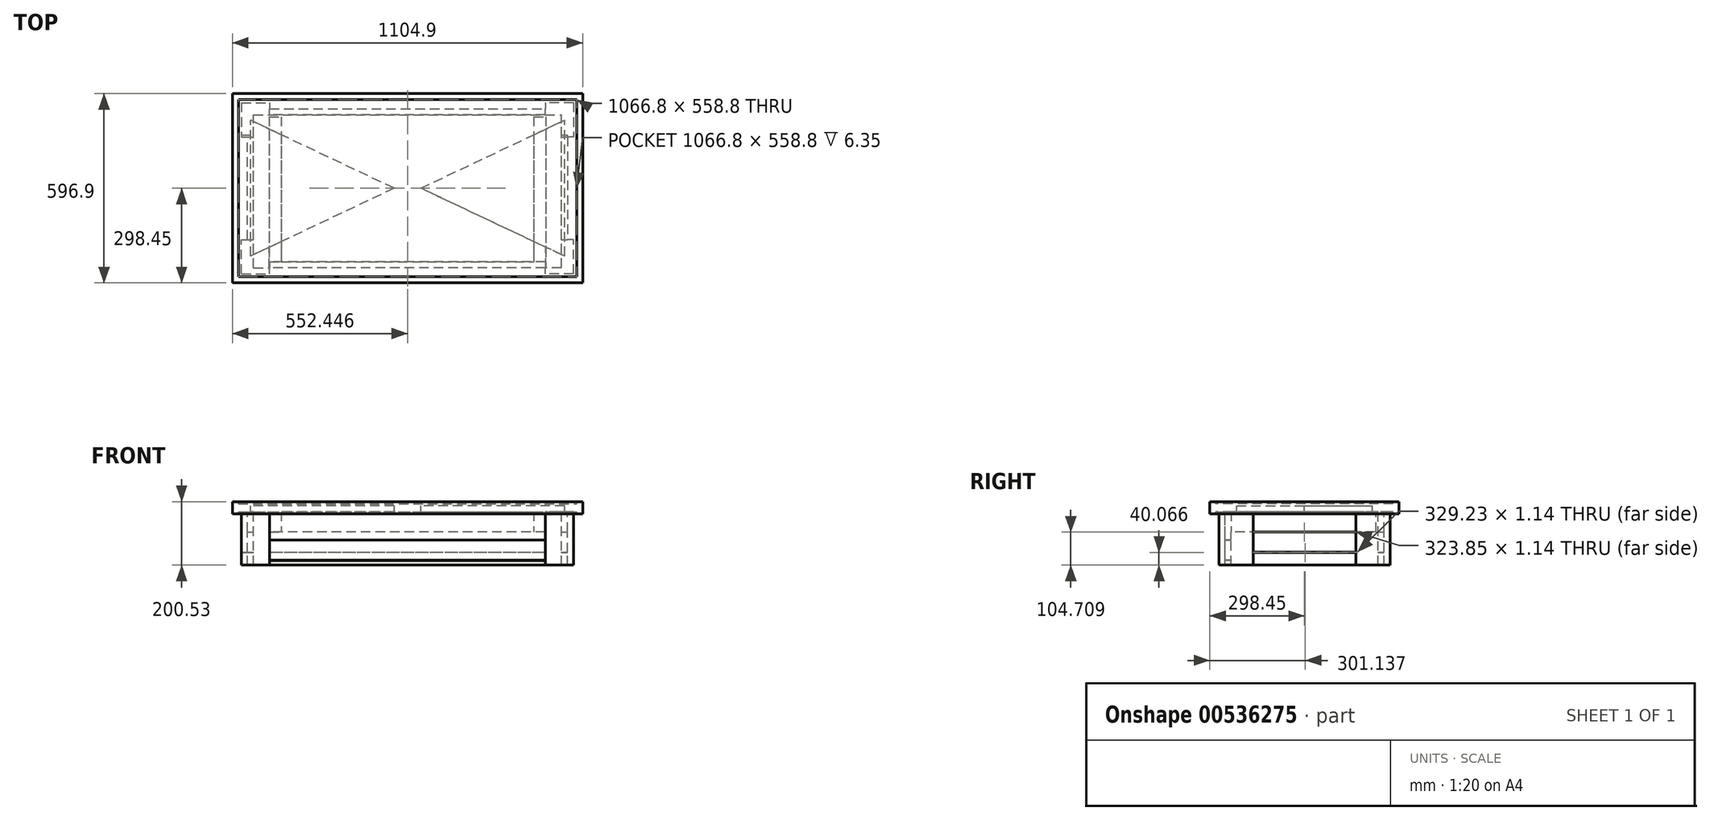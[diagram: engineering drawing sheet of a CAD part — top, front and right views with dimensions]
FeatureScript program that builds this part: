
annotation { "Feature Type Name" : "Feature", "Feature Type Description" : "" }
export const myFeature = defineFeature(function(context is Context, id is Id, definition is map)
    precondition{}
    {
        {
            var Q0;
            Q0=qCreatedBy(makeId("Top.planeOp"),FACE);
            var sketch = newSketch(context, id + "F0", { "sketchPlane" : qUnion([Q0])});
            skLineSegment(sketch, "E0.bottom", {"start": v(-500.95, 298.2) * mm, "end": v(565.85, 298.2) * mm});
            skLineSegment(sketch, "E0.top", {"start": v(-500.95, -260.6) * mm, "end": v(565.85, -260.6) * mm});
            skLineSegment(sketch, "E0.left", {"start": v(-500.95, 298.2) * mm, "end": v(-500.95, -260.6) * mm});
            skLineSegment(sketch, "E0.right", {"start": v(565.85, 298.2) * mm, "end": v(565.85, -260.6) * mm});
            skSolve(sketch);
        }
        {
            var Q0;
            Q0 = qSketchRegion(id + "F0", true);
            extrude(context, id + "F1", {"entities" : qUnion([Q0]), "depth" : 6.35 * mm, "offsetDistance" : 25.4 * mm});
        }
        {
            var Q0;
            Q0=makeQuery(id+"F1.opExtrude","CAP_FACE",FACE,{"disambiguationData":[OSD([sQuery(id+"F0.wireOp",EDGE,"E0.bottom"),sQuery(id+"F0.wireOp",EDGE,"E0.top"),sQuery(id+"F0.wireOp",EDGE,"E0.left"),sQuery(id+"F0.wireOp",EDGE,"E0.right")])],"isStart":false});
            cPlane(context, id + "F2", {"entities" : qUnion([Q0]), "cplaneType" : CPlaneType.OFFSET, "offset" : 6.35 * mm, "width" : 152.4 * mm, "height" : 152.4 * mm});
        }
        {
            var Q0;
            Q0=qCreatedBy(id+"F2.planeOp",FACE);
            var sketch = newSketch(context, id + "F3", { "sketchPlane" : qUnion([Q0])});
            skLineSegment(sketch, "E1.bottom", {"start": v(-520, 317.26) * mm, "end": v(584.9, 317.26) * mm});
            skLineSegment(sketch, "E1.top", {"start": v(-520, -279.64) * mm, "end": v(584.9, -279.64) * mm});
            skLineSegment(sketch, "E1.left", {"start": v(-520, 317.26) * mm, "end": v(-520, -279.64) * mm});
            skLineSegment(sketch, "E1.right", {"start": v(584.9, 317.26) * mm, "end": v(584.9, -279.64) * mm});
            skLineSegment(sketch, "E2.bottom", {"start": v(-500.95, 298.2) * mm, "end": v(565.85, 298.2) * mm});
            skLineSegment(sketch, "E2.top", {"start": v(-500.95, -260.6) * mm, "end": v(565.85, -260.6) * mm});
            skLineSegment(sketch, "E2.left", {"start": v(-500.95, 298.2) * mm, "end": v(-500.95, -260.6) * mm});
            skLineSegment(sketch, "E2.right", {"start": v(565.85, 298.2) * mm, "end": v(565.85, -260.6) * mm});
            skSolve(sketch);
        }
        {
            var Q0;
            Q0 = qSketchRegion(id + "F3", true);
            extrude(context, id + "F4", {"entities" : qUnion([Q0]), "oppositeDirection" : true, "depth" : 38.1 * mm, "offsetDistance" : 25.4 * mm});
        }
        {
            var Q0;
            Q0=makeQuery(id+"F1.opExtrude","CAP_FACE",FACE,{"disambiguationData":[OSD([sQuery(id+"F0.wireOp",EDGE,"E0.bottom"),sQuery(id+"F0.wireOp",EDGE,"E0.top"),sQuery(id+"F0.wireOp",EDGE,"E0.left"),sQuery(id+"F0.wireOp",EDGE,"E0.right")])],"isStart":true});
            var sketch = newSketch(context, id + "F5", { "sketchPlane" : qUnion([Q0])});
            skLineSegment(sketch, "E3.bottom", {"start": v(565.85, 260.6) * mm, "end": v(-500.95, 260.6) * mm});
            skLineSegment(sketch, "E3.top", {"start": v(565.85, -298.2) * mm, "end": v(-500.95, -298.2) * mm});
            skLineSegment(sketch, "E3.left", {"start": v(565.85, 260.6) * mm, "end": v(565.85, -298.2) * mm});
            skLineSegment(sketch, "E3.right", {"start": v(-500.95, 260.6) * mm, "end": v(-500.95, -298.2) * mm});
            skLineSegment(sketch, "E4.bottom", {"start": v(500.82, 222.5) * mm, "end": v(-435.93, 222.5) * mm});
            skLineSegment(sketch, "E4.top", {"start": v(500.82, -260.1) * mm, "end": v(-435.93, -260.1) * mm});
            skLineSegment(sketch, "E4.left", {"start": v(527.75, 195.57) * mm, "end": v(527.75, -233.19) * mm});
            skLineSegment(sketch, "E4.right", {"start": v(-462.85, 195.57) * mm, "end": v(-462.85, -233.19) * mm});
            skLineSegment(sketch, "E5", {"start": v(527.75, 195.57) * mm, "end": v(74.38, -18.8) * mm});
            skLineSegment(sketch, "E6", {"start": v(500.82, 222.5) * mm, "end": v(32.45, 1.02) * mm});
            skLineSegment(sketch, "E7", {"start": v(-435.93, 222.5) * mm, "end": v(32.45, 1.02) * mm});
            skLineSegment(sketch, "E8", {"start": v(500.82, -260.1) * mm, "end": v(32.45, -38.64) * mm});
            skLineSegment(sketch, "E9.trimOffspring", {"start": v(-9.49, -18.8) * mm, "end": v(-462.85, 195.57) * mm});
            skLineSegment(sketch, "E10.trimOffspring", {"start": v(74.38, -18.8) * mm, "end": v(527.75, -233.19) * mm});
            skLineSegment(sketch, "E11.trimOffspring", {"start": v(32.45, -38.64) * mm, "end": v(-435.93, -260.1) * mm});
            skLineSegment(sketch, "E12.trimOffspring", {"start": v(-9.49, -18.8) * mm, "end": v(-462.85, -233.19) * mm});
            skPoint(sketch, "E13.orphan", {"position": v(-462.85, -260.1) * mm});
            skPoint(sketch, "E14.orphan", {"position": v(527.75, 222.5) * mm});
            skPoint(sketch, "E15.orphan", {"position": v(527.75, -260.1) * mm});
            skPoint(sketch, "E16.orphan", {"position": v(-462.85, 222.5) * mm});
            skSolve(sketch);
        }
        {
            var Q0;
            Q0=makeQuery(id+"F5.imprint","IMPRINT",FACE,{"disambiguationData":[TD([[makeQuery(id+"F5.imprint","IMPRINT",EDGE,{"derivedFrom":sQuery(id+"F5.wireOp",EDGE,"E3.bottom")}),-1.0]])]});
            extrude(context, id + "F6", {"entities" : qUnion([Q0]), "depth" : 19.05 * mm, "offsetDistance" : 25.4 * mm});
        }
        {
            var Q0;
            Q0=makeQuery(id+"F6.opExtrude","CAP_FACE",FACE,{"disambiguationData":[OSD([sQuery(id+"F5.wireOp",EDGE,"E3.bottom"),sQuery(id+"F5.wireOp",EDGE,"E3.top"),sQuery(id+"F5.wireOp",EDGE,"E3.left"),sQuery(id+"F5.wireOp",EDGE,"E3.right"),sQuery(id+"F5.wireOp",EDGE,"E4.bottom"),sQuery(id+"F5.wireOp",EDGE,"E4.top"),sQuery(id+"F5.wireOp",EDGE,"E4.left"),sQuery(id+"F5.wireOp",EDGE,"E4.right"),sQuery(id+"F5.wireOp",EDGE,"E5"),sQuery(id+"F5.wireOp",EDGE,"E6"),sQuery(id+"F5.wireOp",EDGE,"E7"),sQuery(id+"F5.wireOp",EDGE,"E8"),sQuery(id+"F5.wireOp",EDGE,"E9.trimOffspring"),sQuery(id+"F5.wireOp",EDGE,"E10.trimOffspring"),sQuery(id+"F5.wireOp",EDGE,"E11.trimOffspring"),sQuery(id+"F5.wireOp",EDGE,"E12.trimOffspring")])],"isStart":false});
            var sketch = newSketch(context, id + "F7", { "sketchPlane" : qUnion([Q0])});
            skLineSegment(sketch, "E17.bottom", {"start": v(-403.8, 232.02) * mm, "end": v(468.7, 232.02) * mm});
            skLineSegment(sketch, "E17.top", {"start": v(-403.8, 212.97) * mm, "end": v(468.7, 212.97) * mm});
            skLineSegment(sketch, "E17.left", {"start": v(-403.8, 232.02) * mm, "end": v(-403.8, 212.97) * mm});
            skLineSegment(sketch, "E17.right", {"start": v(468.7, 232.02) * mm, "end": v(468.7, 212.97) * mm});
            skSolve(sketch);
        }
        {
            var Q0;
            Q0 = qSketchRegion(id + "F7", true);
            extrude(context, id + "F8", {"entities" : qUnion([Q0]), "operationType" : NewBodyOperationType.ADD, "depth" : 88.9 * mm, "offsetDistance" : 25.4 * mm});
        }
        {
            var Q0;
            Q0=makeQuery(id+"F8.opExtrude","SWEPT_FACE",FACE,{"disambiguationData":[OSD([sQuery(id+"F7.wireOp",EDGE,"E17.top")])]});
            var sketch = newSketch(context, id + "F9", { "sketchPlane" : qUnion([Q0])});
            skLineSegment(sketch, "E18.bottom", {"start": v(403.8, -19.05) * mm, "end": v(365.7, -19.05) * mm});
            skLineSegment(sketch, "E18.top", {"start": v(403.8, -82.55) * mm, "end": v(365.7, -82.55) * mm});
            skLineSegment(sketch, "E18.left", {"start": v(403.8, -19.05) * mm, "end": v(403.8, -82.55) * mm});
            skLineSegment(sketch, "E18.right", {"start": v(365.7, -19.05) * mm, "end": v(365.7, -82.55) * mm});
            skLineSegment(sketch, "E19.bottom", {"start": v(-468.7, -19.05) * mm, "end": v(-430.6, -19.05) * mm});
            skLineSegment(sketch, "E19.top", {"start": v(-468.7, -82.55) * mm, "end": v(-430.6, -82.55) * mm});
            skLineSegment(sketch, "E19.left", {"start": v(-468.7, -19.05) * mm, "end": v(-468.7, -82.55) * mm});
            skLineSegment(sketch, "E19.right", {"start": v(-430.6, -19.05) * mm, "end": v(-430.6, -82.55) * mm});
            skSolve(sketch);
        }
        {
            var Q0;
            Q0 = qSketchRegion(id + "F9", true);
            extrude(context, id + "F10", {"entities" : qUnion([Q0]), "operationType" : NewBodyOperationType.ADD, "depth" : 457.2 * mm, "offsetDistance" : 25.4 * mm});
        }
        {
            var Q0;
            {var subQ2=sQuery(id+"F5.wireOp",EDGE,"E12.trimOffspring");var subQ3=sQuery(id+"F5.wireOp",EDGE,"E11.trimOffspring");var subQ4=sQuery(id+"F5.wireOp",EDGE,"E10.trimOffspring");var subQ5=sQuery(id+"F5.wireOp",EDGE,"E9.trimOffspring");var subQ6=sQuery(id+"F5.wireOp",EDGE,"E8");var subQ7=sQuery(id+"F5.wireOp",EDGE,"E7");var subQ9=sQuery(id+"F5.wireOp",EDGE,"E3.left");var subQ10=sQuery(id+"F5.wireOp",EDGE,"E3.top");var subQ13=sQuery(id+"F5.wireOp",EDGE,"E3.right");var subQ14=sQuery(id+"F5.wireOp",EDGE,"E3.bottom");var subQ15=sQuery(id+"F5.wireOp",EDGE,"E6");var subQ16=sQuery(id+"F5.wireOp",EDGE,"E4.bottom");var subQ17=sQuery(id+"F5.wireOp",EDGE,"E4.top");var subQ18=sQuery(id+"F5.wireOp",EDGE,"E4.left");var subQ19=sQuery(id+"F5.wireOp",EDGE,"E4.right");var subQ20=sQuery(id+"F5.wireOp",EDGE,"E5");Q0=makeQuery(id+"F10.boolean.opBoolean","SPLIT",FACE,{"disambiguationData":[TD([makeQuery(id+"F6.opExtrude","SWEPT_FACE",FACE,{"disambiguationData":[OSD([subQ14])]})])],"derivedFrom":makeQuery(id+"F6.opExtrude","CAP_FACE",FACE,{"disambiguationData":[OSD([subQ14,subQ10,subQ9,subQ13,subQ16,subQ17,subQ18,subQ19,subQ20,subQ15,subQ7,subQ6,subQ5,subQ4,subQ3,subQ2])],"isStart":false})});}
            var sketch = newSketch(context, id + "F11", { "sketchPlane" : qUnion([Q0])});
            skLineSegment(sketch, "E20.bottom", {"start": v(-491.43, 251.07) * mm, "end": v(-402.53, 251.07) * mm});
            skLineSegment(sketch, "E20.top", {"start": v(-491.43, 232.02) * mm, "end": v(-402.53, 232.02) * mm});
            skLineSegment(sketch, "E20.left", {"start": v(-491.43, 251.07) * mm, "end": v(-491.43, 232.02) * mm});
            skLineSegment(sketch, "E20.right", {"start": v(-402.53, 251.07) * mm, "end": v(-402.53, 232.02) * mm});
            skLineSegment(sketch, "E21.bottom", {"start": v(-491.43, 232.02) * mm, "end": v(-472.38, 232.02) * mm});
            skLineSegment(sketch, "E21.top", {"start": v(-491.43, 143.12) * mm, "end": v(-472.38, 143.12) * mm});
            skLineSegment(sketch, "E21.left", {"start": v(-491.43, 232.02) * mm, "end": v(-491.43, 143.12) * mm});
            skLineSegment(sketch, "E21.right", {"start": v(-472.38, 232.02) * mm, "end": v(-472.38, 143.12) * mm});
            skLineSegment(sketch, "E22", {"start": v(-9.49, -18.8) * mm, "end": v(32.45, -18.8) * mm});
            skLineSegment(sketch, "E23", {"start": v(32.45, -18.8) * mm, "end": v(32.45, 108.2) * mm});
            skLineSegment(sketch, "E24.MirrorCS", {"start": v(-491.43, -288.68) * mm, "end": v(-491.43, -269.63) * mm});
            skLineSegment(sketch, "E25.MirrorCS", {"start": v(-491.43, -269.63) * mm, "end": v(-472.38, -269.63) * mm});
            skLineSegment(sketch, "E26.MirrorCS", {"start": v(-472.38, -269.63) * mm, "end": v(-472.38, -180.73) * mm});
            skLineSegment(sketch, "E27.MirrorCS", {"start": v(-491.43, -180.73) * mm, "end": v(-472.38, -180.73) * mm});
            skLineSegment(sketch, "E28.MirrorCS", {"start": v(-491.43, -269.63) * mm, "end": v(-491.43, -180.73) * mm});
            skLineSegment(sketch, "E29.MirrorCS", {"start": v(-491.43, -269.63) * mm, "end": v(-402.53, -269.63) * mm});
            skLineSegment(sketch, "E30.MirrorCS", {"start": v(-402.53, -288.68) * mm, "end": v(-402.53, -269.63) * mm});
            skLineSegment(sketch, "E31.MirrorCS", {"start": v(-491.43, -288.68) * mm, "end": v(-402.53, -288.68) * mm});
            skLineSegment(sketch, "E32.MirrorCS", {"start": v(556.32, -288.68) * mm, "end": v(467.42, -288.68) * mm});
            skLineSegment(sketch, "E33.MirrorCS", {"start": v(556.32, -288.68) * mm, "end": v(556.32, -269.63) * mm});
            skLineSegment(sketch, "E34.MirrorCS", {"start": v(556.32, -269.63) * mm, "end": v(467.42, -269.63) * mm});
            skLineSegment(sketch, "E35.MirrorCS", {"start": v(467.42, -288.68) * mm, "end": v(467.42, -269.63) * mm});
            skLineSegment(sketch, "E36.MirrorCS", {"start": v(537.27, -269.63) * mm, "end": v(537.27, -180.73) * mm});
            skLineSegment(sketch, "E37.MirrorCS", {"start": v(556.32, -269.63) * mm, "end": v(556.32, -180.73) * mm});
            skLineSegment(sketch, "E38.MirrorCS", {"start": v(556.32, -180.73) * mm, "end": v(537.27, -180.73) * mm});
            skLineSegment(sketch, "E39.MirrorCS", {"start": v(556.32, 143.12) * mm, "end": v(537.27, 143.12) * mm});
            skLineSegment(sketch, "E40.MirrorCS", {"start": v(556.32, 232.02) * mm, "end": v(556.32, 143.12) * mm});
            skLineSegment(sketch, "E41.MirrorCS", {"start": v(537.27, 232.02) * mm, "end": v(537.27, 143.12) * mm});
            skLineSegment(sketch, "E42.MirrorCS", {"start": v(556.32, 232.02) * mm, "end": v(467.42, 232.02) * mm});
            skLineSegment(sketch, "E43.MirrorCS", {"start": v(556.32, 251.07) * mm, "end": v(467.42, 251.07) * mm});
            skLineSegment(sketch, "E44.MirrorCS", {"start": v(556.32, 251.07) * mm, "end": v(556.32, 232.02) * mm});
            skLineSegment(sketch, "E45.MirrorCS", {"start": v(467.42, 251.07) * mm, "end": v(467.42, 232.02) * mm});
            skSolve(sketch);
        }
        {
            var Q0;
            Q0 = qSketchRegion(id + "F11", true);
            extrude(context, id + "F12", {"entities" : qUnion([Q0]), "operationType" : NewBodyOperationType.ADD, "depth" : 419.1 * mm, "offsetDistance" : 25.4 * mm});
        }
        {
            var Q0;
            {var subQ2=sQuery(id+"F5.wireOp",EDGE,"E12.trimOffspring");var subQ3=sQuery(id+"F5.wireOp",EDGE,"E11.trimOffspring");var subQ4=sQuery(id+"F5.wireOp",EDGE,"E10.trimOffspring");var subQ5=sQuery(id+"F5.wireOp",EDGE,"E9.trimOffspring");var subQ6=sQuery(id+"F5.wireOp",EDGE,"E8");var subQ7=sQuery(id+"F5.wireOp",EDGE,"E7");var subQ9=sQuery(id+"F5.wireOp",EDGE,"E3.left");var subQ10=sQuery(id+"F5.wireOp",EDGE,"E3.top");var subQ13=sQuery(id+"F5.wireOp",EDGE,"E3.right");var subQ14=sQuery(id+"F5.wireOp",EDGE,"E3.bottom");var subQ15=sQuery(id+"F5.wireOp",EDGE,"E6");var subQ16=sQuery(id+"F5.wireOp",EDGE,"E4.bottom");var subQ17=sQuery(id+"F5.wireOp",EDGE,"E4.top");var subQ18=sQuery(id+"F5.wireOp",EDGE,"E4.left");var subQ19=sQuery(id+"F5.wireOp",EDGE,"E4.right");var subQ20=sQuery(id+"F5.wireOp",EDGE,"E5");Q0=makeQuery(id+"F10.boolean.opBoolean","SPLIT",FACE,{"disambiguationData":[TD([makeQuery(id+"F6.opExtrude","SWEPT_FACE",FACE,{"disambiguationData":[OSD([subQ14])]})])],"derivedFrom":makeQuery(id+"F6.opExtrude","CAP_FACE",FACE,{"disambiguationData":[OSD([subQ14,subQ10,subQ9,subQ13,subQ16,subQ17,subQ18,subQ19,subQ20,subQ15,subQ7,subQ6,subQ5,subQ4,subQ3,subQ2])],"isStart":false})});}
            var sketch = newSketch(context, id + "F13", { "sketchPlane" : qUnion([Q0])});
            skLineSegment(sketch, "E46.bottom", {"start": v(-472.38, 232.02) * mm, "end": v(-453.33, 232.02) * mm});
            skLineSegment(sketch, "E46.top", {"start": v(-472.38, -269.63) * mm, "end": v(537.27, -269.63) * mm});
            skLineSegment(sketch, "E46.left", {"start": v(-472.38, 232.02) * mm, "end": v(-472.38, -269.63) * mm});
            skLineSegment(sketch, "E46.right", {"start": v(537.27, 232.02) * mm, "end": v(537.27, -269.63) * mm});
            skLineSegment(sketch, "E47.top", {"start": v(-453.33, -250.58) * mm, "end": v(518.22, -250.58) * mm});
            skLineSegment(sketch, "E47.left", {"start": v(-453.33, 212.97) * mm, "end": v(-453.33, -250.58) * mm});
            skLineSegment(sketch, "E47.right", {"start": v(518.22, 212.97) * mm, "end": v(518.22, -250.58) * mm});
            skLineSegment(sketch, "E48", {"start": v(518.22, 212.97) * mm, "end": v(518.22, 232.02) * mm});
            skLineSegment(sketch, "E49", {"start": v(-453.33, 212.97) * mm, "end": v(-453.33, 232.02) * mm});
            skLineSegment(sketch, "E50.trimOffspring", {"start": v(518.22, 232.02) * mm, "end": v(537.27, 232.02) * mm});
            skSolve(sketch);
        }
        {
            var Q0;
            Q0 = qSketchRegion(id + "F13", true);
            extrude(context, id + "F14", {"entities" : qUnion([Q0]), "operationType" : NewBodyOperationType.ADD, "depth" : 192.79 * mm, "offsetDistance" : 25.4 * mm});
        }
        {
            var Q0;
            Q0=makeQuery(id+"F14.opExtrude","SWEPT_FACE",FACE,{"disambiguationData":[OSD([sQuery(id+"F13.wireOp",EDGE,"E46.right")])]});
            var sketch = newSketch(context, id + "F15", { "sketchPlane" : qUnion([Q0])});
            skLineSegment(sketch, "E51.bottom", {"start": v(-143.12, -82.55) * mm, "end": v(180.73, -82.55) * mm});
            skLineSegment(sketch, "E51.top", {"start": v(-143.12, -83.7) * mm, "end": v(180.73, -83.7) * mm});
            skLineSegment(sketch, "E51.left", {"start": v(-143.12, -82.55) * mm, "end": v(-143.12, -83.7) * mm});
            skLineSegment(sketch, "E51.right", {"start": v(180.73, -82.55) * mm, "end": v(180.73, -83.7) * mm});
            skLineSegment(sketch, "E52.bottom", {"start": v(-143.12, -147.2) * mm, "end": v(186.1, -147.2) * mm});
            skLineSegment(sketch, "E52.top", {"start": v(-143.12, -148.34) * mm, "end": v(186.1, -148.34) * mm});
            skLineSegment(sketch, "E52.left", {"start": v(-143.12, -147.2) * mm, "end": v(-143.12, -148.34) * mm});
            skLineSegment(sketch, "E52.right", {"start": v(186.1, -147.2) * mm, "end": v(186.1, -148.34) * mm});
            skSolve(sketch);
        }
        {
            var Q0;
            Q0 = qSketchRegion(id + "F15", true);
            extrude(context, id + "F16", {"entities" : qUnion([Q0]), "operationType" : NewBodyOperationType.REMOVE, "oppositeDirection" : true, "depth" : 1219.2 * mm, "offsetDistance" : 25.4 * mm});
        }
        {
            var Q0;
            Q0=makeQuery(id+"F14.opExtrude","SWEPT_FACE",FACE,{"disambiguationData":[OSD([sQuery(id+"F13.wireOp",EDGE,"E46.top")])]});
            var sketch = newSketch(context, id + "F17", { "sketchPlane" : qUnion([Q0])});
            skLineSegment(sketch, "E53.bottom", {"start": v(-467.42, -147.2) * mm, "end": v(402.53, -147.2) * mm});
            skLineSegment(sketch, "E53.top", {"start": v(-467.42, -148.34) * mm, "end": v(402.53, -148.34) * mm});
            skLineSegment(sketch, "E53.left", {"start": v(-467.42, -148.34) * mm, "end": v(-467.42, -147.2) * mm});
            skLineSegment(sketch, "E53.right", {"start": v(402.53, -148.34) * mm, "end": v(402.53, -147.2) * mm});
            skLineSegment(sketch, "E54.right", {"start": v(402.53, -84.96) * mm, "end": v(402.53, -115.44) * mm});
            skLineSegment(sketch, "E55.bottom", {"start": v(402.53, -82.55) * mm, "end": v(-467.42, -82.55) * mm});
            skLineSegment(sketch, "E55.top", {"start": v(402.53, -83.7) * mm, "end": v(-467.42, -83.7) * mm});
            skLineSegment(sketch, "E55.left", {"start": v(402.53, -82.55) * mm, "end": v(402.53, -83.7) * mm});
            skLineSegment(sketch, "E55.right", {"start": v(-467.42, -82.55) * mm, "end": v(-467.42, -83.7) * mm});
            skSolve(sketch);
        }
        {
            var Q0;
            Q0 = qSketchRegion(id + "F17", true);
            extrude(context, id + "F18", {"entities" : qUnion([Q0]), "operationType" : NewBodyOperationType.REMOVE, "oppositeDirection" : true, "depth" : 25.4 * mm, "offsetDistance" : 25.4 * mm});
        }
        {
            var Q0;
            Q0=makeQuery(id+"F8.opExtrude","CAP_FACE",FACE,{"disambiguationData":[OSD([sQuery(id+"F7.wireOp",EDGE,"E17.bottom"),sQuery(id+"F7.wireOp",EDGE,"E17.top"),sQuery(id+"F7.wireOp",EDGE,"E17.left"),sQuery(id+"F7.wireOp",EDGE,"E17.right")])],"isStart":false});
            cPlane(context, id + "F19", {"entities" : qUnion([Q0]), "cplaneType" : CPlaneType.OFFSET, "offset" : 1.14 * mm, "width" : 152.4 * mm, "height" : 152.4 * mm});
        }
        {
            var Q0;
            Q0=qCreatedBy(id+"F19.planeOp",FACE);
            var sketch = newSketch(context, id + "F20", { "sketchPlane" : qUnion([Q0])});
            skLineSegment(sketch, "E56.bottom", {"start": v(468.7, 212.97) * mm, "end": v(-403.8, 212.97) * mm});
            skLineSegment(sketch, "E56.top", {"start": v(468.7, 232.02) * mm, "end": v(-403.8, 232.02) * mm});
            skLineSegment(sketch, "E56.left", {"start": v(468.7, 212.97) * mm, "end": v(468.7, 232.02) * mm});
            skLineSegment(sketch, "E56.right", {"start": v(-403.8, 212.97) * mm, "end": v(-403.8, 232.02) * mm});
            skSolve(sketch);
        }
        {
            var Q0;
            Q0 = qSketchRegion(id + "F20", true);
            extrude(context, id + "F21", {"entities" : qUnion([Q0]), "operationType" : NewBodyOperationType.ADD, "depth" : 128.14 * mm, "offsetDistance" : 25.4 * mm});
        }
        {
            var Q0;
            Q0=makeQuery(id+"F21.opExtrude","SWEPT_FACE",FACE,{"disambiguationData":[OSD([sQuery(id+"F20.wireOp",EDGE,"E56.top")])]});
            var sketch = newSketch(context, id + "F22", { "sketchPlane" : qUnion([Q0])});
            skLineSegment(sketch, "E57.bottom", {"start": v(-402.53, -172.6) * mm, "end": v(467.42, -172.6) * mm});
            skLineSegment(sketch, "E57.top", {"start": v(-402.53, -173.74) * mm, "end": v(467.42, -173.74) * mm});
            skLineSegment(sketch, "E57.left", {"start": v(-402.53, -172.6) * mm, "end": v(-402.53, -173.74) * mm});
            skLineSegment(sketch, "E57.right", {"start": v(467.42, -172.6) * mm, "end": v(467.42, -173.74) * mm});
            skSolve(sketch);
        }
        {
            var Q0;
            Q0 = qSketchRegion(id + "F22", true);
            extrude(context, id + "F23", {"entities" : qUnion([Q0]), "operationType" : NewBodyOperationType.REMOVE, "oppositeDirection" : true, "depth" : 25.4 * mm, "offsetDistance" : 25.4 * mm});
        }
        {
            var Q0;
            Q0=makeQuery(id+"F14.opExtrude","CAP_FACE",FACE,{"disambiguationData":[OSD([sQuery(id+"F13.wireOp",EDGE,"E46.bottom"),sQuery(id+"F13.wireOp",EDGE,"E46.top"),sQuery(id+"F13.wireOp",EDGE,"E46.left"),sQuery(id+"F13.wireOp",EDGE,"E46.right"),sQuery(id+"F13.wireOp",EDGE,"E47.top"),sQuery(id+"F13.wireOp",EDGE,"E47.left"),sQuery(id+"F13.wireOp",EDGE,"E47.right"),sQuery(id+"F13.wireOp",EDGE,"E48"),sQuery(id+"F13.wireOp",EDGE,"E49"),sQuery(id+"F13.wireOp",EDGE,"E50.trimOffspring")])],"isStart":false});
            var sketch = newSketch(context, id + "F24", { "sketchPlane" : qUnion([Q0])});
            skLineSegment(sketch, "E58.bottom", {"start": v(-472.38, -269.63) * mm, "end": v(-434.28, -269.63) * mm});
            skLineSegment(sketch, "E58.top", {"start": v(-472.38, -180.73) * mm, "end": v(-434.28, -180.73) * mm});
            skLineSegment(sketch, "E58.left", {"start": v(-472.38, -269.63) * mm, "end": v(-472.38, -180.73) * mm});
            skLineSegment(sketch, "E58.right", {"start": v(-434.28, -269.63) * mm, "end": v(-434.28, -180.73) * mm});
            skLineSegment(sketch, "E59.bottom", {"start": v(-472.38, 232.02) * mm, "end": v(-434.28, 232.02) * mm});
            skLineSegment(sketch, "E59.top", {"start": v(-472.38, 143.12) * mm, "end": v(-434.28, 143.12) * mm});
            skLineSegment(sketch, "E59.left", {"start": v(-472.38, 232.02) * mm, "end": v(-472.38, 143.12) * mm});
            skLineSegment(sketch, "E59.right", {"start": v(-434.28, 232.02) * mm, "end": v(-434.28, 143.12) * mm});
            skLineSegment(sketch, "E60.bottom", {"start": v(537.27, -269.63) * mm, "end": v(499.17, -269.63) * mm});
            skLineSegment(sketch, "E60.top", {"start": v(537.27, -180.73) * mm, "end": v(499.17, -180.73) * mm});
            skLineSegment(sketch, "E60.left", {"start": v(537.27, -269.63) * mm, "end": v(537.27, -180.73) * mm});
            skLineSegment(sketch, "E60.right", {"start": v(499.17, -269.63) * mm, "end": v(499.17, -180.73) * mm});
            skLineSegment(sketch, "E61.bottom", {"start": v(537.27, 232.02) * mm, "end": v(499.17, 232.02) * mm});
            skLineSegment(sketch, "E61.top", {"start": v(537.27, 143.12) * mm, "end": v(499.17, 143.12) * mm});
            skLineSegment(sketch, "E61.left", {"start": v(537.27, 232.02) * mm, "end": v(537.27, 143.12) * mm});
            skLineSegment(sketch, "E61.right", {"start": v(499.17, 232.02) * mm, "end": v(499.17, 143.12) * mm});
            skSolve(sketch);
        }
        {
            var Q0;
            Q0 = qSketchRegion(id + "F24", true);
            var Q1;
            Q1=makeQuery(id+"F12.opExtrude","CAP_FACE",FACE,{"disambiguationData":[OSD([sQuery(id+"F11.wireOp",EDGE,"E39.MirrorCS"),sQuery(id+"F11.wireOp",EDGE,"E40.MirrorCS"),sQuery(id+"F11.wireOp",EDGE,"E41.MirrorCS"),sQuery(id+"F11.wireOp",EDGE,"E42.MirrorCS"),sQuery(id+"F11.wireOp",EDGE,"E43.MirrorCS"),sQuery(id+"F11.wireOp",EDGE,"E44.MirrorCS"),sQuery(id+"F11.wireOp",EDGE,"E45.MirrorCS")])],"isStart":false});
            extrude(context, id + "F25", {"entities" : qUnion([Q0]), "operationType" : NewBodyOperationType.ADD, "endBound" : BoundingType.UP_TO_SURFACE, "depth" : 25.4 * mm, "endBoundEntityFace" : qUnion([Q1]), "offsetDistance" : 25.4 * mm});
        }
        {
            var Q0;
            Q0=makeQuery(id+"F12.opExtrude","SWEPT_FACE",FACE,{"disambiguationData":[OSD([sQuery(id+"F11.wireOp",EDGE,"E24.MirrorCS"),sQuery(id+"F11.wireOp",EDGE,"E28.MirrorCS")])]});
            var sketch = newSketch(context, id + "F26", { "sketchPlane" : qUnion([Q0])});
            skLineSegment(sketch, "E62.bottom", {"start": v(-295.03, -187.83) * mm, "end": v(263.77, -187.83) * mm});
            skLineSegment(sketch, "E62.top", {"start": v(-295.03, -568.83) * mm, "end": v(263.77, -568.83) * mm});
            skLineSegment(sketch, "E62.left", {"start": v(-295.03, -187.83) * mm, "end": v(-295.03, -568.83) * mm});
            skLineSegment(sketch, "E62.right", {"start": v(263.77, -187.83) * mm, "end": v(263.77, -568.83) * mm});
            skSolve(sketch);
        }
        {
            var Q0;
            Q0 = qSketchRegion(id + "F26", true);
            extrude(context, id + "F27", {"entities" : qUnion([Q0]), "operationType" : NewBodyOperationType.REMOVE, "oppositeDirection" : true, "depth" : 1397 * mm, "offsetDistance" : 25.4 * mm});
        }
        {
            var Q0;
            {var subQ1=sQuery(id+"F5.wireOp",EDGE,"E4.left");var subQ5=sQuery(id+"F5.wireOp",EDGE,"E4.bottom");var subQ6=makeQuery(id+"F5.imprint","INTERSECT",VERTEX,{"derivedFrom":[subQ5,subQ1]});Q0=makeQuery(id+"F5.imprint","IMPRINT",FACE,{"disambiguationData":[TD([[makeQuery(id+"F5.imprint","IMPRINT",EDGE,{"disambiguationData":[TD([[subQ6,-1.0]])],"derivedFrom":subQ5}),1.0]])]});}
            var Q1;
            {var subQ1=sQuery(id+"F5.wireOp",EDGE,"E4.left");var subQ7=sQuery(id+"F5.wireOp",EDGE,"E4.top");var subQ8=makeQuery(id+"F5.imprint","INTERSECT",VERTEX,{"derivedFrom":[subQ7,subQ1]});Q1=makeQuery(id+"F5.imprint","IMPRINT",FACE,{"disambiguationData":[TD([[makeQuery(id+"F5.imprint","IMPRINT",EDGE,{"disambiguationData":[TD([[subQ8,-1.0]])],"derivedFrom":subQ7}),-1.0]])]});}
            var Q2;
            {var subQ1=sQuery(id+"F5.wireOp",EDGE,"E4.right");var subQ6=sQuery(id+"F5.wireOp",EDGE,"E4.top");var subQ9=makeQuery(id+"F5.imprint","INTERSECT",VERTEX,{"derivedFrom":[subQ6,subQ1]});Q2=makeQuery(id+"F5.imprint","IMPRINT",FACE,{"disambiguationData":[TD([[makeQuery(id+"F5.imprint","IMPRINT",EDGE,{"disambiguationData":[TD([[subQ9,1.0]])],"derivedFrom":subQ6}),-1.0]])]});}
            var Q3;
            {var subQ1=sQuery(id+"F5.wireOp",EDGE,"E4.bottom");var subQ7=sQuery(id+"F5.wireOp",EDGE,"E4.right");var subQ8=makeQuery(id+"F5.imprint","INTERSECT",VERTEX,{"derivedFrom":[subQ1,subQ7]});Q3=makeQuery(id+"F5.imprint","IMPRINT",FACE,{"disambiguationData":[TD([[makeQuery(id+"F5.imprint","IMPRINT",EDGE,{"disambiguationData":[TD([[subQ8,1.0]])],"derivedFrom":subQ1}),1.0]])]});}
            var Q4;
            {var subQ0=sQuery(id+"F5.wireOp",EDGE,"E7");var subQ1=sQuery(id+"F5.wireOp",EDGE,"E5");var subQ2=makeQuery(id+"F5.imprint","INTERSECT",VERTEX,{"derivedFrom":[subQ1,subQ0]});Q4=makeQuery(id+"F5.imprint","IMPRINT",FACE,{"disambiguationData":[TD([[makeQuery(id+"F5.imprint","IMPRINT",EDGE,{"disambiguationData":[TD([[subQ2,-1.0]])],"derivedFrom":subQ1}),-1.0]])]});}
            extrude(context, id + "F28", {"entities" : qUnion([Q0, Q1, Q2, Q3, Q4]), "operationType" : NewBodyOperationType.ADD, "depth" : 19.05 * mm, "offsetDistance" : 25.4 * mm});
        }
    });
